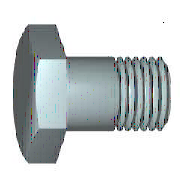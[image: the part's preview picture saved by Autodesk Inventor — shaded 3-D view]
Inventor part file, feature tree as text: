
AUTODESK INVENTOR PART (.ipt)
format: ipt  version: 2021 (Build 250183000, 183)  size: 190,464 bytes
history: native  units: mm (DEFAULTED — no unit token found)
features: sketch x3, extrude x1, chamfer x1, plane x1
ambient origin geometry x7: Origin, YZ Plane, XZ Plane, X Axis, Y Axis, Z Axis, Center Point
bodies: Solid1 (feature_tree), Body (feature_tree)
feature tree (6):
  extrude  "Head"  Depth=26.0mm
  chamfer  "Chamfer1"  Distance=5.8mm
  plane  "Work Plane1"
  sketch  "Sketch1"  dims[d0=80.0mm d1=26.0mm]
  sketch  "Sketch2"  dims[d2=10.0mm]
  sketch  "Sketch4"  dims[d12=90.0deg d3=5.8mm d4=0.0mm d5=30.0deg d21=90.0deg d6=0.920175mm d7=0.920275mm d8=0.0mm d9=0.6001mm d10=14.63mm d11=16.0mm d13=0.920275mm d14=10.0mm d15=26.0mm d16=0.0mm d19=16.0mm d55=45.0deg d57=0.0mm d58=0.0mm]
